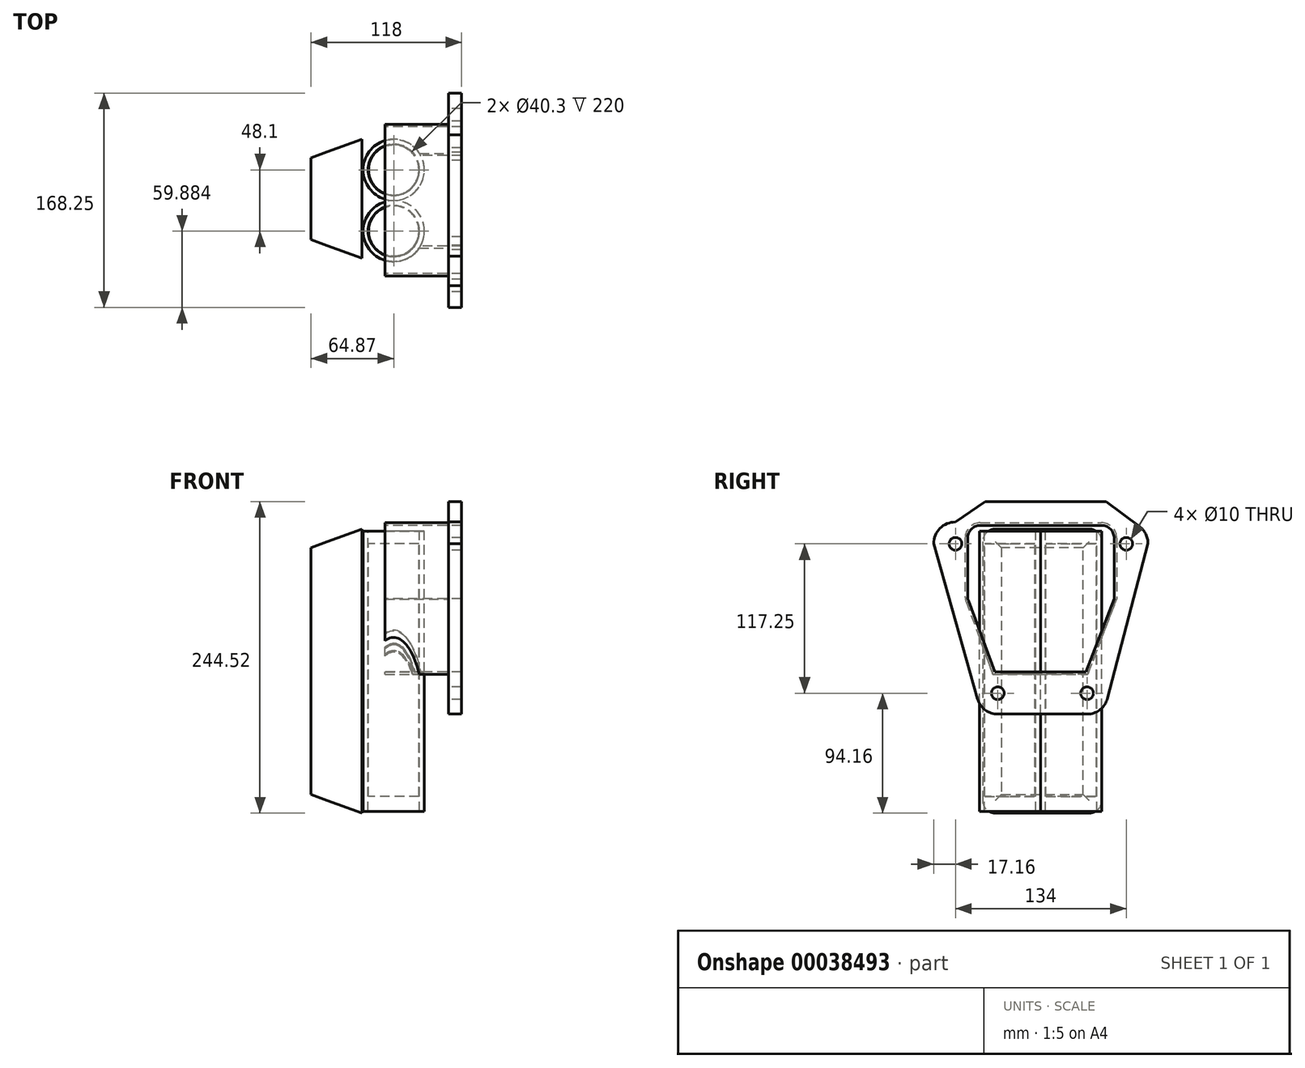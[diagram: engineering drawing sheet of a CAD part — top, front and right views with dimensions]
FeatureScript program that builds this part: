
annotation { "Feature Type Name" : "Feature", "Feature Type Description" : "" }
export const myFeature = defineFeature(function(context is Context, id is Id, definition is map)
    precondition{}
    {
        {
            var Q0;
            Q0=qCreatedBy(makeId("Right.planeOp"),FACE);
            var sketch = newSketch(context, id + "F0", { "sketchPlane" : qUnion([Q0])});
            skCircle(sketch, "E0", {"center": v(0, 0) * mm, "radius": 5 * mm});
            skCircle(sketch, "E1", {"center": v(134, 0) * mm, "radius": 5 * mm});
            skCircle(sketch, "E2", {"center": v(33.25, -117.25) * mm, "radius": 5 * mm});
            skCircle(sketch, "E3", {"center": v(103.25, -117.25) * mm, "radius": 5 * mm});
            skArc(sketch, "E4", {"start": v(0, 17.16) * mm, "mid": v(-14.98, 8.36) * mm, "end": v(-14.6, -9) * mm});
            skArc(sketch, "E5", {"start": v(17.38, -121.75) * mm, "mid": v(23.93, -130.86) * mm, "end": v(34.79, -133.68) * mm});
            skArc(sketch, "E6", {"start": v(101.71, -133.68) * mm, "mid": v(112.7, -130.77) * mm, "end": v(119.2, -121.44) * mm});
            skArc(sketch, "E7", {"start": v(148.89, -8.4) * mm, "mid": v(150.73, 3.53) * mm, "end": v(144.23, 13.7) * mm});
            skLineSegment(sketch, "E8", {"start": v(-17.16, 0) * mm, "end": v(17.38, -121.75) * mm});
            skLineSegment(sketch, "E9", {"start": v(31.71, -133.68) * mm, "end": v(104.79, -133.68) * mm});
            skLineSegment(sketch, "E10", {"start": v(151.1, 0) * mm, "end": v(119.2, -121.44) * mm});
            skLineSegment(sketch, "E11", {"start": v(0, 17.16) * mm, "end": v(23.19, 33.11) * mm});
            skLineSegment(sketch, "E12", {"start": v(23.19, 33.11) * mm, "end": v(118.24, 33.11) * mm});
            skLineSegment(sketch, "E13", {"start": v(118.24, 33.11) * mm, "end": v(144.23, 13.7) * mm});
            skLineSegment(sketch, "E14.bottom", {"start": v(19.56, 14.5) * mm, "end": v(114.56, 14.5) * mm});
            skLineSegment(sketch, "E14.left", {"start": v(9.56, 4.5) * mm, "end": v(9.56, -41.2) * mm});
            skLineSegment(sketch, "E14.right", {"start": v(124.56, 4.5) * mm, "end": v(124.56, -43) * mm});
            skLineSegment(sketch, "E15", {"start": v(10.18, -44.68) * mm, "end": v(30.9, -100.5) * mm});
            skLineSegment(sketch, "E16", {"start": v(30.9, -100.5) * mm, "end": v(102.26, -100.5) * mm});
            skLineSegment(sketch, "E17", {"start": v(102.26, -100.5) * mm, "end": v(124.56, -43) * mm});
            skPoint(sketch, "E18.orphan", {"position": v(124.56, -100.5) * mm});
            skPoint(sketch, "E14.top.start.orphan", {"position": v(9.56, -100.5) * mm});
            skPoint(sketch, "E19.visualSharp", {"position": v(9.56, 14.5) * mm});
            skArc(sketch, "E19.filletArc", {"start": v(19.56, 14.5) * mm, "mid": v(12.49, 11.57) * mm, "end": v(9.56, 4.5) * mm});
            skPoint(sketch, "E20.visualSharp", {"position": v(124.56, 14.5) * mm});
            skArc(sketch, "E20.filletArc", {"start": v(124.56, 4.5) * mm, "mid": v(121.63, 11.57) * mm, "end": v(114.56, 14.5) * mm});
            skPoint(sketch, "E21.visualSharp", {"position": v(9.56, -43) * mm});
            skArc(sketch, "E21.filletArc", {"start": v(9.56, -41.2) * mm, "mid": v(9.72, -42.97) * mm, "end": v(10.18, -44.68) * mm});
            skSolve(sketch);
        }
        {
            var Q0;
            Q0=makeQuery(id+"F0.imprint","IMPRINT",FACE,{"disambiguationData":[TD([[makeQuery(id+"F0.imprint","IMPRINT",EDGE,{"derivedFrom":sQuery(id+"F0.wireOp",EDGE,"E0")}),-1.0]])]});
            extrude(context, id + "F1", {"entities" : qUnion([Q0]), "depth" : 10 * mm});
        }
        {
            var Q0;
            Q0=qCreatedBy(makeId("Top.planeOp"),FACE);
            var sketch = newSketch(context, id + "F2", { "sketchPlane" : qUnion([Q0])});
            skCircle(sketch, "E22", {"center": v(-68.13, 57.72) * mm, "radius": 19.75 * mm});
            skCircle(sketch, "E23", {"center": v(-68.13, 57.72) * mm, "radius": 24 * mm});
            skCircle(sketch, "E24", {"center": v(-68.13, 57.72) * mm, "radius": 20.15 * mm});
            skCircle(sketch, "E25", {"center": v(-68.13, 105.82) * mm, "radius": 24 * mm});
            skCircle(sketch, "E26", {"center": v(-68.13, 105.82) * mm, "radius": 20.15 * mm});
            skCircle(sketch, "E27", {"center": v(-68.13, 105.82) * mm, "radius": 19.75 * mm});
            skSolve(sketch);
        }
        {
            var Q0;
            Q0=makeQuery(id+"F2.imprint","IMPRINT",FACE,{"disambiguationData":[TD([[makeQuery(id+"F2.imprint","IMPRINT",EDGE,{"derivedFrom":sQuery(id+"F2.wireOp",EDGE,"E27")}),1.0]])]});
            var Q1;
            Q1=makeQuery(id+"F2.imprint","IMPRINT",FACE,{"disambiguationData":[TD([[makeQuery(id+"F2.imprint","IMPRINT",EDGE,{"derivedFrom":sQuery(id+"F2.wireOp",EDGE,"E22")}),1.0]])]});
            extrude(context, id + "F3", {"entities" : qUnion([Q0, Q1]), "oppositeDirection" : true, "depth" : 198.2 * mm});
        }
        {
            var Q0;
            Q0 = qSketchRegion(id + "F2", true);
            extrude(context, id + "F4", {"entities" : qUnion([Q0]), "oppositeDirection" : true, "depth" : 210 * mm, "hasSecondDirection" : true, "secondDirectionOppositeDirection" : false, "secondDirectionDepth" : 10 * mm});
        }
        {
            var Q0;
            Q0=makeQuery(id+"F3.opExtrude","SWEPT_BODY",BODY,{"disambiguationData":[OSD([sQuery(id+"F2.wireOp",EDGE,"E27")])]});
            var Q1;
            Q1=makeQuery(id+"F4.opExtrude","SWEPT_BODY",BODY,{"disambiguationData":[OSD([sQuery(id+"F2.wireOp",EDGE,"E25"),sQuery(id+"F2.wireOp",EDGE,"E26")])]});
            var Q2;
            Q2=makeQuery(id+"F4.opExtrude","SWEPT_BODY",BODY,{"disambiguationData":[OSD([sQuery(id+"F2.wireOp",EDGE,"E23"),sQuery(id+"F2.wireOp",EDGE,"E24")])]});
            var Q3;
            Q3=makeQuery(id+"F3.opExtrude","SWEPT_BODY",BODY,{"disambiguationData":[OSD([sQuery(id+"F2.wireOp",EDGE,"E22")])]});
            transform(context, id + "F5", {"entities" : qUnion([Q0, Q1, Q2, Q3]), "transformType" : TransformType.TRANSLATION_3D, "dx" : 25 * mm, "dy" : -15 * mm, "dz" : 0 * mm, "makeCopy" : false});
        }
        {
            var Q0;
            Q0=makeQuery(id+"F1.opExtrude","CAP_FACE",FACE,{"disambiguationData":[OSD([sQuery(id+"F0.wireOp",EDGE,"E0"),sQuery(id+"F0.wireOp",EDGE,"E1"),sQuery(id+"F0.wireOp",EDGE,"E2"),sQuery(id+"F0.wireOp",EDGE,"E3"),sQuery(id+"F0.wireOp",EDGE,"E4"),sQuery(id+"F0.wireOp",EDGE,"E5"),sQuery(id+"F0.wireOp",EDGE,"E6"),sQuery(id+"F0.wireOp",EDGE,"E7"),sQuery(id+"F0.wireOp",EDGE,"E8"),sQuery(id+"F0.wireOp",EDGE,"E9"),sQuery(id+"F0.wireOp",EDGE,"E10"),sQuery(id+"F0.wireOp",EDGE,"E11"),sQuery(id+"F0.wireOp",EDGE,"E12"),sQuery(id+"F0.wireOp",EDGE,"E13"),sQuery(id+"F0.wireOp",EDGE,"E14.bottom"),sQuery(id+"F0.wireOp",EDGE,"E14.left"),sQuery(id+"F0.wireOp",EDGE,"E14.right"),sQuery(id+"F0.wireOp",EDGE,"E15"),sQuery(id+"F0.wireOp",EDGE,"E17"),sQuery(id+"F0.wireOp",EDGE,"E16"),sQuery(id+"F0.wireOp",EDGE,"E19.filletArc"),sQuery(id+"F0.wireOp",EDGE,"E20.filletArc"),sQuery(id+"F0.wireOp",EDGE,"E21.filletArc")])],"isStart":true});
            var sketch = newSketch(context, id + "F6", { "sketchPlane" : qUnion([Q0])});
            skLineSegment(sketch, "E28.0", {"start": v(-9.56, 4.5) * mm, "end": v(-9.56, -41.2) * mm});
            skLineSegment(sketch, "E28.1", {"start": v(-10.18, -44.68) * mm, "end": v(-30.9, -100.5) * mm});
            skArc(sketch, "E28.2", {"start": v(-9.56, -41.2) * mm, "mid": v(-9.72, -42.97) * mm, "end": v(-10.18, -44.68) * mm});
            skLineSegment(sketch, "E28.3", {"start": v(-30.9, -100.5) * mm, "end": v(-102.26, -100.5) * mm});
            skLineSegment(sketch, "E28.4", {"start": v(-19.56, 14.5) * mm, "end": v(-114.56, 14.5) * mm});
            skArc(sketch, "E28.5", {"start": v(-19.56, 14.5) * mm, "mid": v(-12.49, 11.57) * mm, "end": v(-9.56, 4.5) * mm});
            skArc(sketch, "E28.6", {"start": v(-124.56, 4.5) * mm, "mid": v(-121.63, 11.57) * mm, "end": v(-114.56, 14.5) * mm});
            skLineSegment(sketch, "E28.7", {"start": v(-124.56, 4.5) * mm, "end": v(-124.56, -43) * mm});
            skLineSegment(sketch, "E28.8", {"start": v(-102.26, -100.5) * mm, "end": v(-124.56, -43) * mm});
            skArc(sketch, "E29.0", {"start": v(-19.56, 16.5) * mm, "mid": v(-11.07, 12.99) * mm, "end": v(-7.56, 4.5) * mm});
            skLineSegment(sketch, "E29.1", {"start": v(-19.56, 16.5) * mm, "end": v(-114.56, 16.5) * mm});
            skLineSegment(sketch, "E29.2", {"start": v(-7.56, 4.5) * mm, "end": v(-7.56, -41.2) * mm});
            skArc(sketch, "E29.3", {"start": v(-126.56, 4.5) * mm, "mid": v(-123.05, 12.99) * mm, "end": v(-114.56, 16.5) * mm});
            skLineSegment(sketch, "E29.4", {"start": v(-126.56, 4.5) * mm, "end": v(-126.56, -43.37) * mm});
            skArc(sketch, "E29.5", {"start": v(-7.56, -41.2) * mm, "mid": v(-7.75, -43.33) * mm, "end": v(-8.3, -45.38) * mm});
            skLineSegment(sketch, "E29.6", {"start": v(-8.3, -45.38) * mm, "end": v(-29.5, -102.5) * mm});
            skLineSegment(sketch, "E29.7", {"start": v(-29.5, -102.5) * mm, "end": v(-103.63, -102.5) * mm});
            skLineSegment(sketch, "E29.8", {"start": v(-103.63, -102.5) * mm, "end": v(-126.56, -43.37) * mm});
            skSolve(sketch);
        }
        {
            var Q0;
            Q0=makeQuery(id+"F6.imprint","IMPRINT",FACE,{"disambiguationData":[TD([[makeQuery(id+"F6.imprint","IMPRINT",EDGE,{"derivedFrom":sQuery(id+"F6.wireOp",EDGE,"E28.0")}),1.0]])]});
            extrude(context, id + "F7", {"entities" : qUnion([Q0]), "operationType" : NewBodyOperationType.ADD, "depth" : 50 * mm});
        }
        {
            var Q0;
            Q0=makeQuery(id+"F1.opExtrude","CAP_FACE",FACE,{"disambiguationData":[OSD([sQuery(id+"F0.wireOp",EDGE,"E0"),sQuery(id+"F0.wireOp",EDGE,"E1"),sQuery(id+"F0.wireOp",EDGE,"E2"),sQuery(id+"F0.wireOp",EDGE,"E3"),sQuery(id+"F0.wireOp",EDGE,"E4"),sQuery(id+"F0.wireOp",EDGE,"E5"),sQuery(id+"F0.wireOp",EDGE,"E6"),sQuery(id+"F0.wireOp",EDGE,"E7"),sQuery(id+"F0.wireOp",EDGE,"E8"),sQuery(id+"F0.wireOp",EDGE,"E9"),sQuery(id+"F0.wireOp",EDGE,"E10"),sQuery(id+"F0.wireOp",EDGE,"E11"),sQuery(id+"F0.wireOp",EDGE,"E12"),sQuery(id+"F0.wireOp",EDGE,"E13"),sQuery(id+"F0.wireOp",EDGE,"E14.bottom"),sQuery(id+"F0.wireOp",EDGE,"E14.left"),sQuery(id+"F0.wireOp",EDGE,"E14.right"),sQuery(id+"F0.wireOp",EDGE,"E15"),sQuery(id+"F0.wireOp",EDGE,"E17"),sQuery(id+"F0.wireOp",EDGE,"E16"),sQuery(id+"F0.wireOp",EDGE,"E19.filletArc"),sQuery(id+"F0.wireOp",EDGE,"E20.filletArc"),sQuery(id+"F0.wireOp",EDGE,"E21.filletArc")])],"isStart":true});
            cPlane(context, id + "F8", {"entities" : qUnion([Q0]), "cplaneType" : CPlaneType.OFFSET, "offset" : 68 * mm, "width" : 150 * mm, "height" : 150 * mm});
        }
        {
            var Q0;
            Q0=qCreatedBy(id+"F8.planeOp",FACE);
            var sketch = newSketch(context, id + "F9", { "sketchPlane" : qUnion([Q0])});
            skLineSegment(sketch, "E30.bottom", {"start": v(-104.85, 61.6) * mm, "end": v(-31.37, 61.6) * mm});
            skLineSegment(sketch, "E30.top", {"start": v(-104.85, -161.41) * mm, "end": v(-31.37, -161.41) * mm});
            skLineSegment(sketch, "E30.left", {"start": v(-114.85, 51.6) * mm, "end": v(-114.85, -151.41) * mm});
            skLineSegment(sketch, "E30.right", {"start": v(-21.37, 51.6) * mm, "end": v(-21.37, -151.41) * mm});
            skLineSegment(sketch, "E31.0", {"start": v(-102.85, 59.6) * mm, "end": v(-33.37, 59.6) * mm});
            skLineSegment(sketch, "E31.1", {"start": v(-112.85, 49.6) * mm, "end": v(-112.85, -149.41) * mm});
            skLineSegment(sketch, "E31.2", {"start": v(-102.85, -159.41) * mm, "end": v(-33.37, -159.41) * mm});
            skLineSegment(sketch, "E31.3", {"start": v(-23.37, 49.6) * mm, "end": v(-23.37, -149.41) * mm});
            skPoint(sketch, "E32.visualSharp", {"position": v(-23.37, 59.6) * mm});
            skArc(sketch, "E32.filletArc", {"start": v(-23.37, 49.6) * mm, "mid": v(-26.3, 56.67) * mm, "end": v(-33.37, 59.6) * mm});
            skPoint(sketch, "E33.visualSharp", {"position": v(-21.37, 61.6) * mm});
            skArc(sketch, "E33.filletArc", {"start": v(-21.37, 51.6) * mm, "mid": v(-24.3, 58.67) * mm, "end": v(-31.37, 61.6) * mm});
            skPoint(sketch, "E34.visualSharp", {"position": v(-23.37, -159.41) * mm});
            skArc(sketch, "E34.filletArc", {"start": v(-33.37, -159.41) * mm, "mid": v(-26.3, -156.48) * mm, "end": v(-23.37, -149.41) * mm});
            skPoint(sketch, "E35.visualSharp", {"position": v(-21.37, -161.41) * mm});
            skArc(sketch, "E35.filletArc", {"start": v(-31.37, -161.41) * mm, "mid": v(-24.3, -158.48) * mm, "end": v(-21.37, -151.41) * mm});
            skPoint(sketch, "E36.visualSharp", {"position": v(-112.85, -159.41) * mm});
            skArc(sketch, "E36.filletArc", {"start": v(-112.85, -149.41) * mm, "mid": v(-109.92, -156.48) * mm, "end": v(-102.85, -159.41) * mm});
            skPoint(sketch, "E37.visualSharp", {"position": v(-114.85, -161.41) * mm});
            skArc(sketch, "E37.filletArc", {"start": v(-114.85, -151.41) * mm, "mid": v(-111.92, -158.48) * mm, "end": v(-104.85, -161.41) * mm});
            skPoint(sketch, "E38.visualSharp", {"position": v(-112.85, 59.6) * mm});
            skArc(sketch, "E38.filletArc", {"start": v(-102.85, 59.6) * mm, "mid": v(-109.92, 56.67) * mm, "end": v(-112.85, 49.6) * mm});
            skPoint(sketch, "E39.visualSharp", {"position": v(-114.85, 61.6) * mm});
            skArc(sketch, "E39.filletArc", {"start": v(-104.85, 61.6) * mm, "mid": v(-111.92, 58.67) * mm, "end": v(-114.85, 51.6) * mm});
            skSolve(sketch);
        }
        {
            var Q0;
            Q0=makeQuery(id+"F9.imprint","IMPRINT",FACE,{"disambiguationData":[TD([[makeQuery(id+"F9.imprint","IMPRINT",EDGE,{"derivedFrom":sQuery(id+"F9.wireOp",EDGE,"E31.0")}),-1.0]])]});
            var Q1;
            Q1=makeQuery(id+"F9.imprint","IMPRINT",FACE,{"disambiguationData":[TD([[makeQuery(id+"F9.imprint","IMPRINT",EDGE,{"derivedFrom":sQuery(id+"F9.wireOp",EDGE,"E30.bottom")}),-1.0]])]});
            extrude(context, id + "F10", {"entities" : qUnion([Q0, Q1]), "depth" : 40 * mm, "hasDraft" : true, "draftAngle" : 20 * degree, "draftPullDirection" : true});
        }
        {
            var Q0;
            Q0=makeQuery(id+"F10.opExtrude","SWEPT_BODY",BODY,{"disambiguationData":[OSD([sQuery(id+"F9.wireOp",EDGE,"E30.bottom"),sQuery(id+"F9.wireOp",EDGE,"E30.top"),sQuery(id+"F9.wireOp",EDGE,"E30.left"),sQuery(id+"F9.wireOp",EDGE,"E30.right"),sQuery(id+"F9.wireOp",EDGE,"E33.filletArc"),sQuery(id+"F9.wireOp",EDGE,"E35.filletArc"),sQuery(id+"F9.wireOp",EDGE,"E37.filletArc"),sQuery(id+"F9.wireOp",EDGE,"E39.filletArc")])]});
            transform(context, id + "F11", {"entities" : qUnion([Q0]), "transformType" : TransformType.TRANSLATION_3D, "dx" : 0 * mm, "dy" : 0 * mm, "dz" : -50 * mm, "makeCopy" : false});
        }
    });
